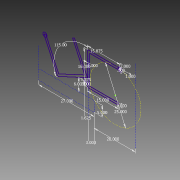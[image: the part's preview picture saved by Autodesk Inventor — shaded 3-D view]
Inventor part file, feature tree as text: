
AUTODESK INVENTOR PART (.ipt)
format: ipt  version: 2014 (Build 180170000, 170)  size: 86,016 bytes
history: native  units: in
note: dims shown in document units (in); Inventor stores cm internally (conversion verified against a paired STEP export)
features: sketch x1
ambient origin geometry x8: Origin, YZ Plane, XZ Plane, XY Plane, X Axis, Y Axis, Z Axis, Center Point
feature tree (1):
  sketch  "Sketch1"  dims[d0=27.0in d1=5.0in d2=25.0in d3=2.0in d5=0.5in d6=1.0in d7=16.0in d8=15.0in d9=1.0in d10=1.0in d11=1.375in d12=2.0in d13=20.0in d14=3.0in d15=6.0in d17=15.875in d18=0.7874in d20=0.7902in d22=1.625in]
